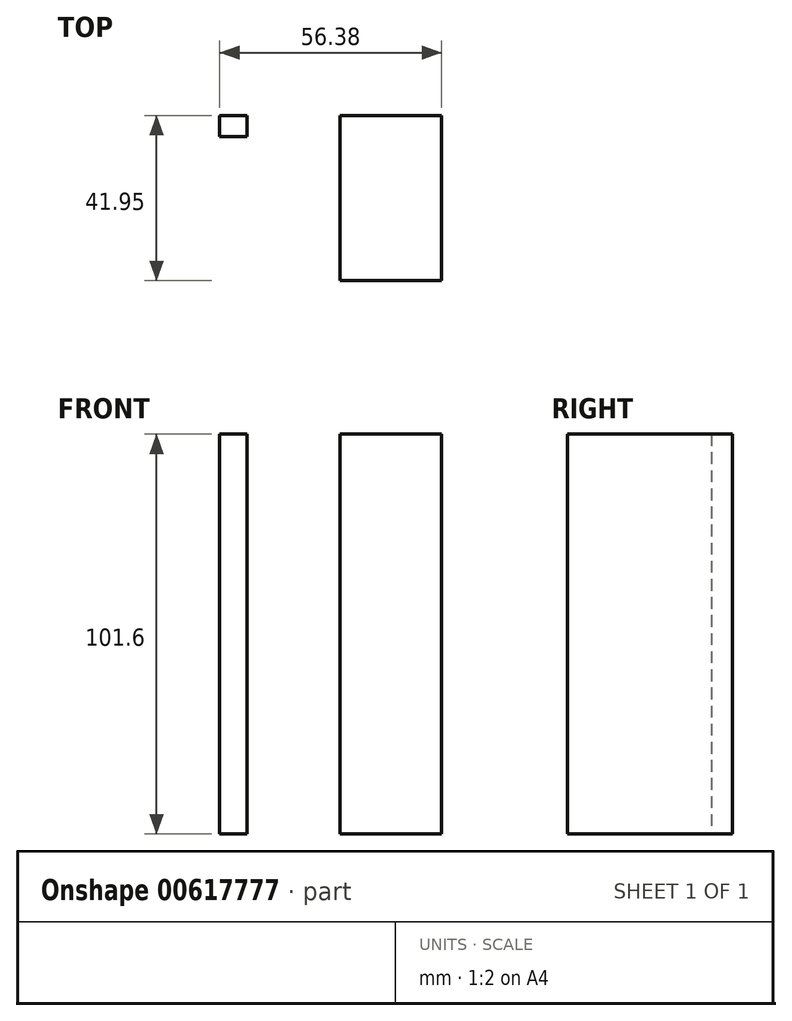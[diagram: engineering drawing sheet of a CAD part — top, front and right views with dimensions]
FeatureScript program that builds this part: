
annotation { "Feature Type Name" : "Feature", "Feature Type Description" : "" }
export const myFeature = defineFeature(function(context is Context, id is Id, definition is map)
    precondition{}
    {
        {
            var Q0;
            Q0=qCreatedBy(makeId("Top.planeOp"),FACE);
            var sketch = newSketch(context, id + "F0", { "sketchPlane" : qUnion([Q0])});
            skLineSegment(sketch, "E0.bottom", {"start": v(-158.1, -20.2) * mm, "end": v(-151.08, -20.2) * mm});
            skLineSegment(sketch, "E0.top", {"start": v(-158.1, -25.57) * mm, "end": v(-151.08, -25.57) * mm});
            skLineSegment(sketch, "E0.left", {"start": v(-158.1, -20.2) * mm, "end": v(-158.1, -25.57) * mm});
            skLineSegment(sketch, "E0.right", {"start": v(-151.08, -20.2) * mm, "end": v(-151.08, -25.57) * mm});
            skLineSegment(sketch, "E1.bottom", {"start": v(-127.52, -20.2) * mm, "end": v(-101.71, -20.2) * mm});
            skLineSegment(sketch, "E1.top", {"start": v(-127.52, -62.16) * mm, "end": v(-101.71, -62.16) * mm});
            skLineSegment(sketch, "E1.left", {"start": v(-127.52, -20.2) * mm, "end": v(-127.52, -62.16) * mm});
            skLineSegment(sketch, "E1.right", {"start": v(-101.71, -20.2) * mm, "end": v(-101.71, -62.16) * mm});
            skSolve(sketch);
        }
        {
            var Q0;
            Q0 = qSketchRegion(id + "F0", true);
            extrude(context, id + "F1", {"entities" : qUnion([Q0]), "depth" : 101.6 * mm, "offsetDistance" : 25.4 * mm});
        }
    });
